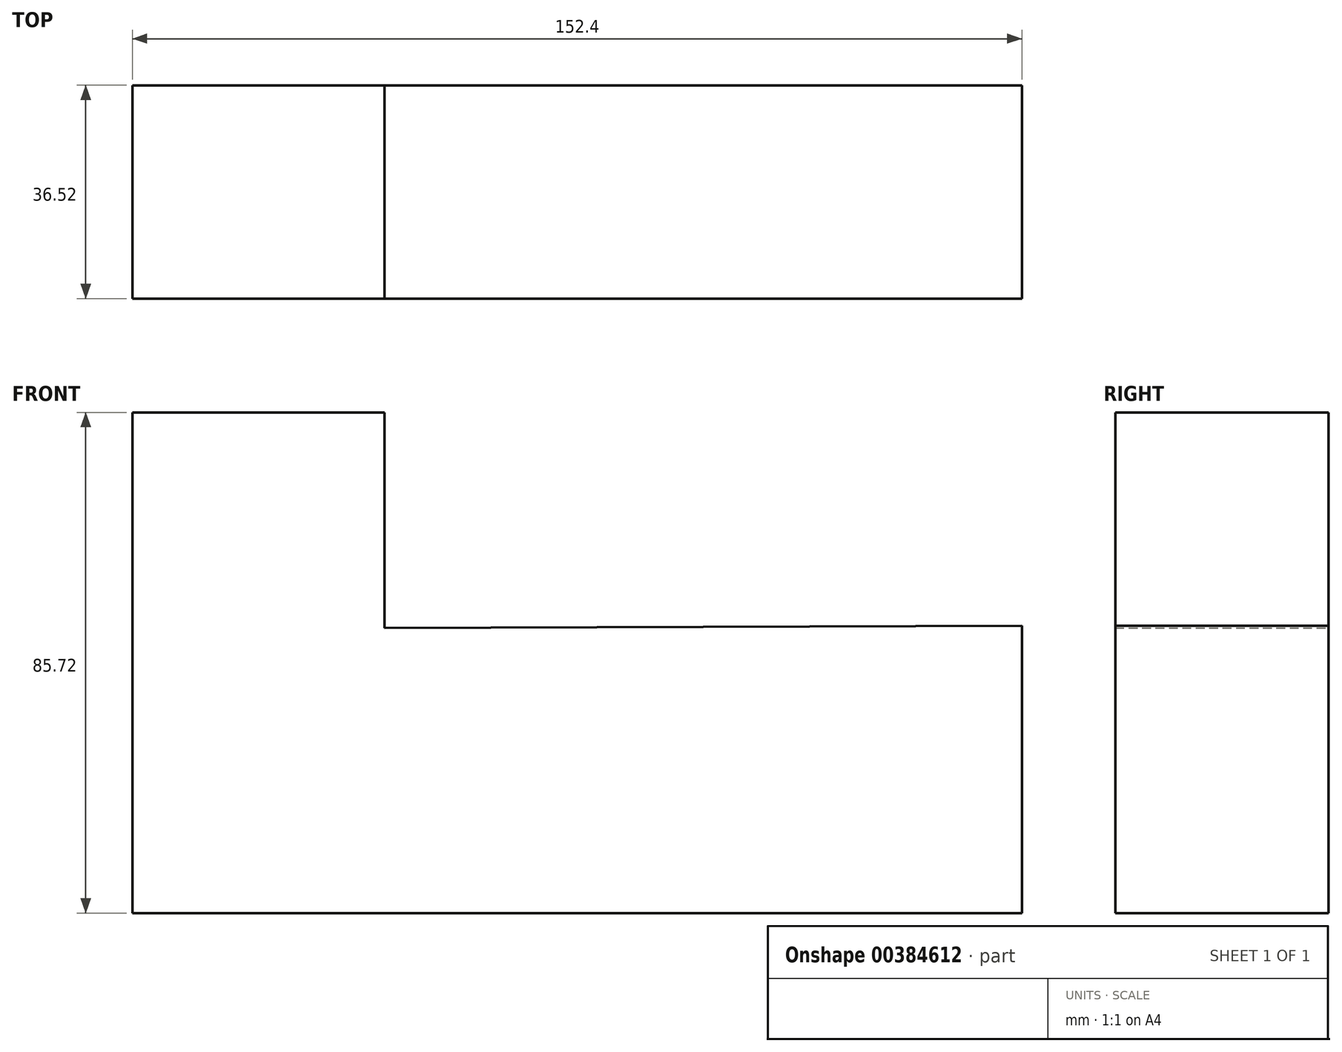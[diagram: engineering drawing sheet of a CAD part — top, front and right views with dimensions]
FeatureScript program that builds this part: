
annotation { "Feature Type Name" : "Feature", "Feature Type Description" : "" }
export const myFeature = defineFeature(function(context is Context, id is Id, definition is map)
    precondition{}
    {
        {
            var Q0;
            Q0=qCreatedBy(makeId("Front.planeOp"),FACE);
            var sketch = newSketch(context, id + "F0", { "sketchPlane" : qUnion([Q0])});
            skLineSegment(sketch, "E0", {"start": v(-76.38, -42.61) * mm, "end": v(76.02, -42.61) * mm});
            skLineSegment(sketch, "E1", {"start": v(76.02, 6.6) * mm, "end": v(76.02, -42.61) * mm});
            skLineSegment(sketch, "E2", {"start": v(-76.38, 43.11) * mm, "end": v(-76.38, -42.61) * mm});
            skLineSegment(sketch, "E3", {"start": v(-33.2, 43.11) * mm, "end": v(-76.38, 43.11) * mm});
            skLineSegment(sketch, "E4", {"start": v(-33.2, 6.22) * mm, "end": v(-33.2, 43.11) * mm});
            skLineSegment(sketch, "E5", {"start": v(-33.2, 6.22) * mm, "end": v(76.02, 6.6) * mm});
            skSolve(sketch);
        }
        {
            var Q0;
            Q0=makeQuery(id+"F0.imprint","IMPRINT",FACE,{"disambiguationData":[TD([[makeQuery(id+"F0.imprint","IMPRINT",EDGE,{"derivedFrom":sQuery(id+"F0.wireOp",EDGE,"E0")}),1.0]])]});
            extrude(context, id + "F1", {"entities" : qUnion([Q0]), "endBound" : BoundingType.SYMMETRIC, "depth" : 36.5 * mm});
        }
    });
